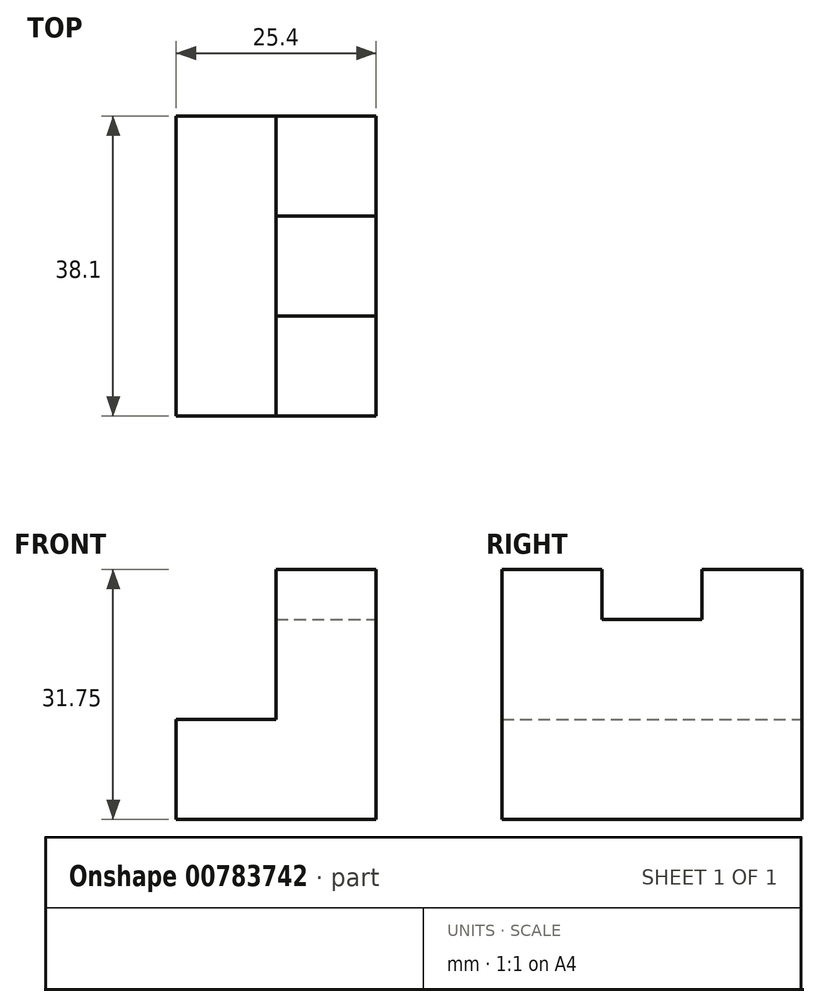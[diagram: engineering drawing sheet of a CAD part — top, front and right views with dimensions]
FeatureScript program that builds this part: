
annotation { "Feature Type Name" : "Feature", "Feature Type Description" : "" }
export const myFeature = defineFeature(function(context is Context, id is Id, definition is map)
    precondition{}
    {
        {
            var Q0;
            Q0=qCreatedBy(makeId("Front.planeOp"),FACE);
            var sketch = newSketch(context, id + "F0", { "sketchPlane" : qUnion([Q0])});
            skLineSegment(sketch, "E0", {"start": v(0, 0) * mm, "end": v(-25.4, 0) * mm});
            skLineSegment(sketch, "E1", {"start": v(-25.4, 0) * mm, "end": v(-25.4, 12.7) * mm});
            skLineSegment(sketch, "E2", {"start": v(-25.4, 12.7) * mm, "end": v(-12.7, 12.7) * mm});
            skLineSegment(sketch, "E3", {"start": v(-12.7, 12.7) * mm, "end": v(-12.7, 31.75) * mm});
            skLineSegment(sketch, "E4", {"start": v(-12.7, 31.75) * mm, "end": v(0, 31.75) * mm});
            skLineSegment(sketch, "E5", {"start": v(0, 31.75) * mm, "end": v(0, 0) * mm});
            skSolve(sketch);
        }
        {
            var Q0;
            Q0=makeQuery(id+"F0.imprint","IMPRINT",FACE,{"disambiguationData":[TD([[makeQuery(id+"F0.imprint","IMPRINT",EDGE,{"derivedFrom":sQuery(id+"F0.wireOp",EDGE,"E0")}),-1.0]])]});
            extrude(context, id + "F1", {"entities" : qUnion([Q0]), "depth" : 38.1 * mm, "offsetDistance" : 25.4 * mm});
        }
        {
            var Q0;
            Q0=makeQuery(id+"F1.opExtrude","SWEPT_FACE",FACE,{"disambiguationData":[OSD([sQuery(id+"F0.wireOp",EDGE,"E5")])]});
            var sketch = newSketch(context, id + "F2", { "sketchPlane" : qUnion([Q0])});
            skLineSegment(sketch, "E6", {"start": v(-38.1, 31.75) * mm, "end": v(-25.4, 31.75) * mm});
            skLineSegment(sketch, "E7", {"start": v(-25.4, 31.75) * mm, "end": v(-25.4, 25.4) * mm});
            skLineSegment(sketch, "E8", {"start": v(-25.4, 25.4) * mm, "end": v(-12.7, 25.4) * mm});
            skLineSegment(sketch, "E9", {"start": v(-12.7, 25.4) * mm, "end": v(-12.7, 31.75) * mm});
            skLineSegment(sketch, "E10", {"start": v(-12.7, 31.75) * mm, "end": v(0, 31.75) * mm});
            skSolve(sketch);
        }
        {
            var Q0;
            {var subQ0=sQuery(id+"F2.wireOp",EDGE,"E7");Q0=makeQuery(id+"F2.imprint","IMPRINT",FACE,{"disambiguationData":[TD([[makeQuery(id+"F2.imprint","IMPRINT",EDGE,{"derivedFrom":subQ0}),1.0]])]});}
            extrude(context, id + "F3", {"entities" : qUnion([Q0]), "operationType" : NewBodyOperationType.REMOVE, "oppositeDirection" : true, "depth" : 12.7 * mm, "offsetDistance" : 25.4 * mm});
        }
    });
